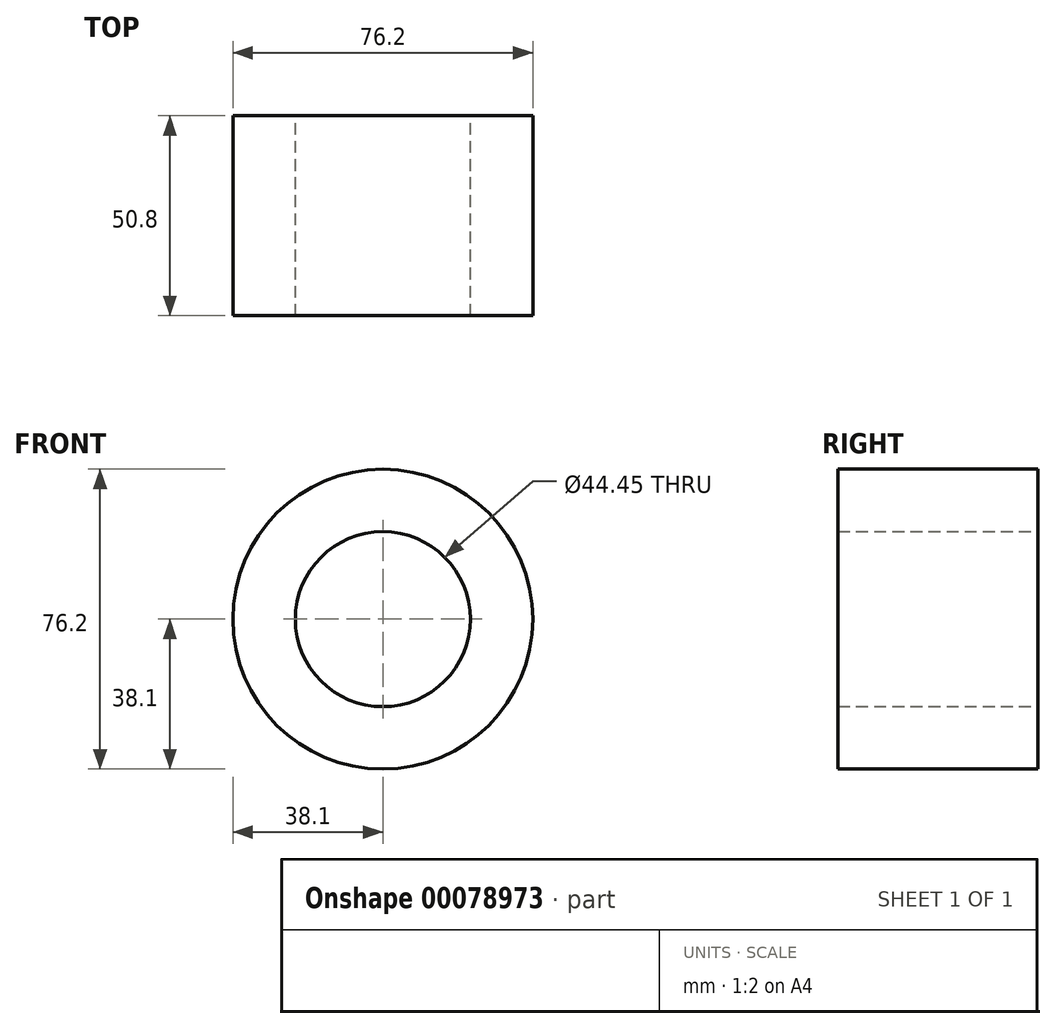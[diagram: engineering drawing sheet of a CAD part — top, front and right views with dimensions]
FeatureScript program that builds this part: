
annotation { "Feature Type Name" : "Feature", "Feature Type Description" : "" }
export const myFeature = defineFeature(function(context is Context, id is Id, definition is map)
    precondition{}
    {
        {
            var Q0;
            Q0=qCreatedBy(makeId("Front.planeOp"),FACE);
            var sketch = newSketch(context, id + "F0", { "sketchPlane" : qUnion([Q0])});
            skCircle(sketch, "E0", {"center": v(0, 0) * mm, "radius": 22.23 * mm});
            skCircle(sketch, "E1", {"center": v(0, 0) * mm, "radius": 38.1 * mm});
            skSolve(sketch);
        }
        {
            var Q0;
            Q0 = qSketchRegion(id + "F0", true);
            extrude(context, id + "F1", {"entities" : qUnion([Q0]), "endBound" : BoundingType.SYMMETRIC, "depth" : 50.8 * mm});
        }
    });
